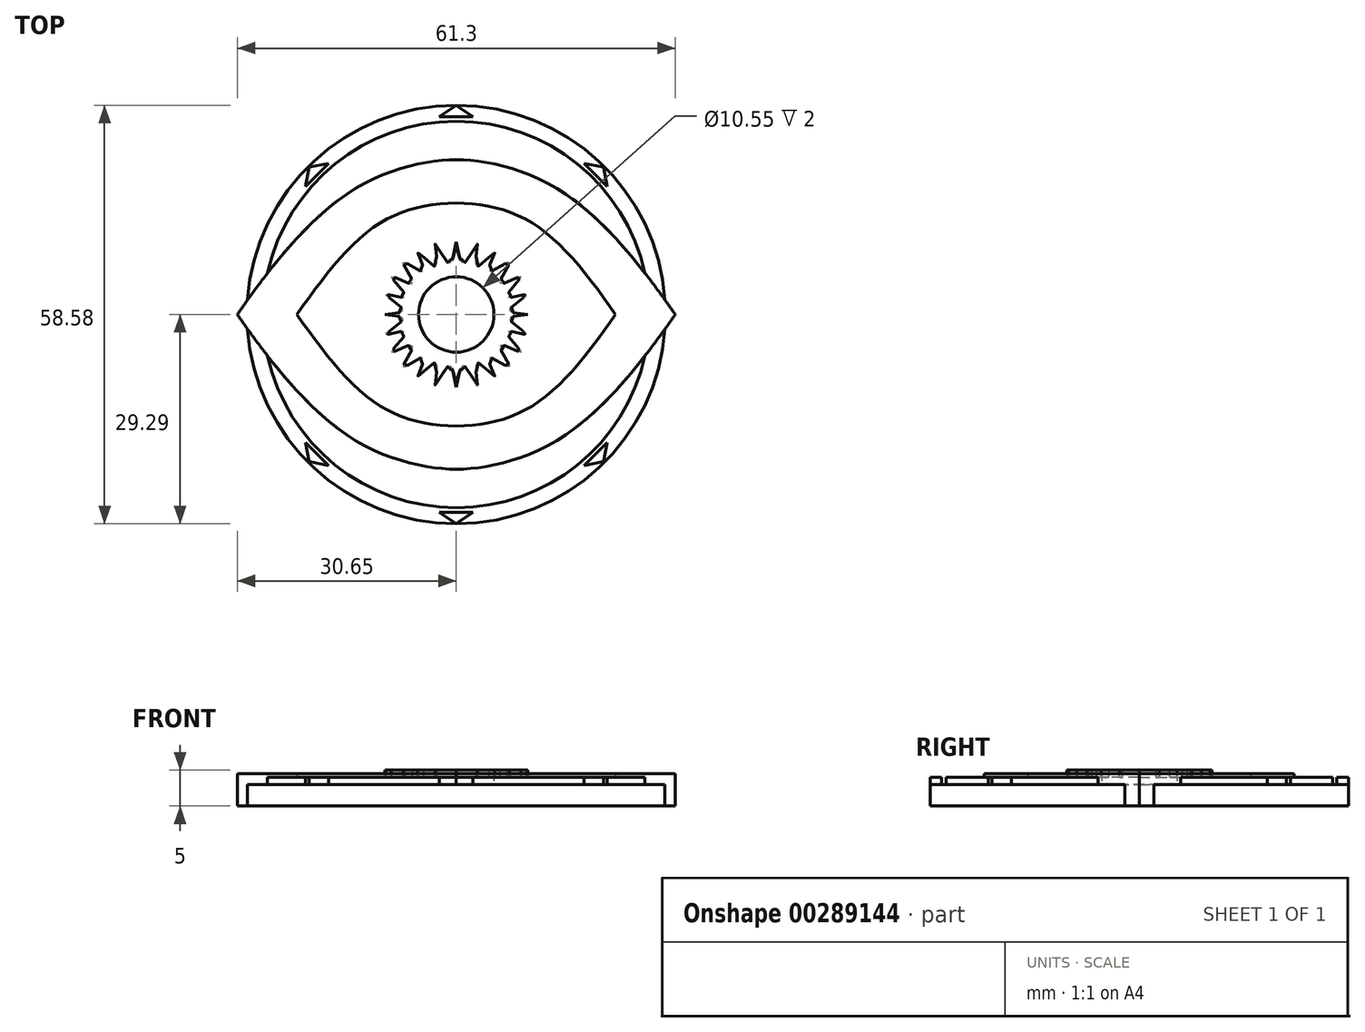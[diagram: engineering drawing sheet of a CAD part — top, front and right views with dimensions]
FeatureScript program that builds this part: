
annotation { "Feature Type Name" : "Feature", "Feature Type Description" : "" }
export const myFeature = defineFeature(function(context is Context, id is Id, definition is map)
    precondition{}
    {
        {
            var Q0;
            Q0=qCreatedBy(makeId("Top.planeOp"),FACE);
            var sketch = newSketch(context, id + "F0", { "sketchPlane" : qUnion([Q0])});
            skArc(sketch, "E0", {"start": v(0, 5.28) * mm, "mid": v(-3.73, 3.73) * mm, "end": v(-5.28, 0) * mm});
            skFitSpline(sketch, "E1", {"points": [v(-10, 0) * mm, v(-7.54, 0.76) * mm, v(-9.83, 2.78) * mm, v(-7.12, 2.5) * mm, v(-9.06, 5.28) * mm, v(-6.15, 4.35) * mm, v(-7.43, 7.33) * mm, v(-4.62, 6.08) * mm, v(-5.38, 8.72) * mm, v(-2.93, 6.76) * mm, v(-2.95, 9.9) * mm, v(-1.17, 7.25) * mm, v(0, 10.15) * mm], "startDerivative": vector(52.2, 3.3) * mm, "endDerivative": vector(8.65, 55.16) * mm});
            skFitSpline(sketch, "E2", {"points": [v(-22.28, 0) * mm, v(-11.02, 12.56) * mm, v(0, 15.6) * mm], "startDerivative": vector(19.04, 27.4) * mm, "endDerivative": vector(26.42, 0.51) * mm});
            skFitSpline(sketch, "E3", {"points": [v(-30.65, 0) * mm, v(-15.05, 17.04) * mm, v(0, 21.68) * mm], "startDerivative": vector(19.04, 27.4) * mm, "endDerivative": vector(26.42, 0.51) * mm});
            skArc(sketch, "E4", {"start": v(0, 27.04) * mm, "mid": v(-19.12, 19.12) * mm, "end": v(-27.04, 0) * mm});
            skArc(sketch, "E5", {"start": v(0, 29.29) * mm, "mid": v(-20.7, 20.7) * mm, "end": v(-29.29, 0) * mm});
            skLineSegment(sketch, "E6", {"start": v(-20.6, 20.6) * mm, "end": v(-21.1, 17.91) * mm});
            skLineSegment(sketch, "E7", {"start": v(-21.1, 17.91) * mm, "end": v(-17.87, 21.15) * mm});
            skLineSegment(sketch, "E8", {"start": v(-17.87, 21.15) * mm, "end": v(-20.6, 20.6) * mm});
            skLineSegment(sketch, "E9", {"start": v(0, 29.29) * mm, "end": v(-2.36, 27.66) * mm});
            skLineSegment(sketch, "E10", {"start": v(-2.36, 27.66) * mm, "end": v(0, 27.66) * mm});
            skLineSegment(sketch, "E11", {"start": v(0, 29.29) * mm, "end": v(0, 0) * mm});
            skLineSegment(sketch, "E12", {"start": v(-30.65, 0) * mm, "end": v(0, 0) * mm});
            skSolve(sketch);
        }
        {
            var Q0;
            {var subQ0=sQuery(id+"F0.wireOp",EDGE,"E0");Q0=makeQuery(id+"F0.imprint","IMPRINT",FACE,{"disambiguationData":[TD([[makeQuery(id+"F0.imprint","IMPRINT",EDGE,{"derivedFrom":subQ0}),1.0]])]});}
            extrude(context, id + "F1", {"entities" : qUnion([Q0]), "depth" : 1 * mm});
        }
        {
            var Q0;
            {var subQ0=sQuery(id+"F0.wireOp",EDGE,"E0");Q0=makeQuery(id+"F0.imprint","IMPRINT",FACE,{"disambiguationData":[TD([[makeQuery(id+"F0.imprint","IMPRINT",EDGE,{"derivedFrom":subQ0}),-1.0]])]});}
            extrude(context, id + "F2", {"entities" : qUnion([Q0]), "operationType" : NewBodyOperationType.ADD, "depth" : 3 * mm});
        }
        {
            var Q0;
            {var subQ0=sQuery(id+"F0.wireOp",EDGE,"E1");Q0=makeQuery(id+"F0.imprint","IMPRINT",FACE,{"disambiguationData":[TD([[makeQuery(id+"F0.imprint","IMPRINT",EDGE,{"derivedFrom":subQ0}),1.0]])]});}
            extrude(context, id + "F3", {"entities" : qUnion([Q0]), "operationType" : NewBodyOperationType.ADD, "depth" : 2 * mm});
        }
        {
            var Q0;
            {var subQ1=sQuery(id+"F0.wireOp",EDGE,"E2");Q0=makeQuery(id+"F0.imprint","IMPRINT",FACE,{"disambiguationData":[TD([[makeQuery(id+"F0.imprint","IMPRINT",EDGE,{"derivedFrom":subQ1}),1.0]])]});}
            var Q1;
            {var subQ0=sQuery(id+"F0.wireOp",EDGE,"E5");var subQ1=sQuery(id+"F0.wireOp",EDGE,"E3");var subQ2=makeQuery(id+"F0.imprint","INTERSECT",VERTEX,{"derivedFrom":[subQ1,subQ0]});Q1=makeQuery(id+"F0.imprint","IMPRINT",FACE,{"disambiguationData":[TD([[makeQuery(id+"F0.imprint","IMPRINT",EDGE,{"disambiguationData":[TD([[subQ2,-1.0]])],"derivedFrom":subQ1}),-1.0]])]});}
            var Q2;
            {var subQ0=sQuery(id+"F0.wireOp",EDGE,"E12");var subQ1=sQuery(id+"F0.wireOp",EDGE,"E3");var subQ2=makeQuery(id+"F0.imprint","INTERSECT",VERTEX,{"derivedFrom":[subQ1,subQ0]});Q2=makeQuery(id+"F0.imprint","IMPRINT",FACE,{"disambiguationData":[TD([[makeQuery(id+"F0.imprint","IMPRINT",EDGE,{"disambiguationData":[TD([[subQ2,-1.0]])],"derivedFrom":subQ1}),-1.0]])]});}
            extrude(context, id + "F4", {"entities" : qUnion([Q0, Q1, Q2]), "operationType" : NewBodyOperationType.ADD, "depth" : 2.5 * mm});
        }
        {
            var Q0;
            {var subQ0=sQuery(id+"F0.wireOp",EDGE,"E11");var subQ1=sQuery(id+"F0.wireOp",EDGE,"E3");var subQ2=makeQuery(id+"F0.imprint","INTERSECT",VERTEX,{"derivedFrom":[subQ1,subQ0]});Q0=makeQuery(id+"F0.imprint","IMPRINT",FACE,{"disambiguationData":[TD([[makeQuery(id+"F0.imprint","IMPRINT",EDGE,{"disambiguationData":[TD([[subQ2,1.0]])],"derivedFrom":subQ1}),1.0]])]});}
            extrude(context, id + "F5", {"entities" : qUnion([Q0]), "operationType" : NewBodyOperationType.ADD, "depth" : 2 * mm});
        }
        {
            var Q0;
            Q0=makeQuery(id+"F0.imprint","IMPRINT",FACE,{"disambiguationData":[TD([[makeQuery(id+"F0.imprint","IMPRINT",EDGE,{"derivedFrom":sQuery(id+"F0.wireOp",EDGE,"E6")}),-1.0]])]});
            extrude(context, id + "F6", {"entities" : qUnion([Q0]), "operationType" : NewBodyOperationType.ADD, "depth" : 1 * mm});
        }
        {
            var Q0;
            Q0=makeQuery(id+"F0.imprint","IMPRINT",FACE,{"disambiguationData":[TD([[makeQuery(id+"F0.imprint","IMPRINT",EDGE,{"derivedFrom":sQuery(id+"F0.wireOp",EDGE,"E6")}),1.0]])]});
            var Q1;
            {var subQ0=sQuery(id+"F0.wireOp",EDGE,"E9");Q1=makeQuery(id+"F0.imprint","IMPRINT",FACE,{"disambiguationData":[TD([[makeQuery(id+"F0.imprint","IMPRINT",EDGE,{"derivedFrom":subQ0}),1.0]])]});}
            extrude(context, id + "F7", {"entities" : qUnion([Q0, Q1]), "operationType" : NewBodyOperationType.ADD, "depth" : 2 * mm});
        }
        {
            var Q0;
            Q0=makeQuery(id+"F1.opExtrude","SWEPT_BODY",BODY,{"disambiguationData":[OSD([sQuery(id+"F0.wireOp",EDGE,"E0"),sQuery(id+"F0.wireOp",EDGE,"E11"),sQuery(id+"F0.wireOp",EDGE,"E12")])]});
            var Q1;
            Q1=qCreatedBy(makeId("Right.planeOp"),FACE);
            mirror(context, id + "F8", {"operationType" : NewBodyOperationType.ADD, "entities" : qUnion([Q0]), "mirrorPlane" : qUnion([Q1])});
        }
        {
            var Q0;
            Q0=makeQuery(id+"F1.opExtrude","SWEPT_BODY",BODY,{"disambiguationData":[OSD([sQuery(id+"F0.wireOp",EDGE,"E0"),sQuery(id+"F0.wireOp",EDGE,"E11"),sQuery(id+"F0.wireOp",EDGE,"E12")])]});
            var Q1;
            Q1=qCreatedBy(makeId("Front.planeOp"),FACE);
            mirror(context, id + "F9", {"operationType" : NewBodyOperationType.ADD, "entities" : qUnion([Q0]), "mirrorPlane" : qUnion([Q1])});
        }
        {
            var Q0;
            {var subQ0=sQuery(id+"F0.wireOp",EDGE,"E11");var subQ1=sQuery(id+"F0.wireOp",EDGE,"E10");var subQ2=sQuery(id+"F0.wireOp",EDGE,"E9");var subQ3=sQuery(id+"F0.wireOp",EDGE,"E8");var subQ4=sQuery(id+"F0.wireOp",EDGE,"E7");var subQ5=sQuery(id+"F0.wireOp",EDGE,"E6");var subQ6=sQuery(id+"F0.wireOp",EDGE,"E4");var subQ7=sQuery(id+"F0.wireOp",EDGE,"E3");var subQ8=sQuery(id+"F0.wireOp",EDGE,"E12");var subQ9=sQuery(id+"F0.wireOp",EDGE,"E2");var subQ10=sQuery(id+"F0.wireOp",EDGE,"E1");var subQ11=sQuery(id+"F0.wireOp",EDGE,"E0");var subQ12=makeQuery(id+"F7.boolean.opBoolean","MERGE",FACE,{"derivedFrom":[makeQuery(id+"F6.boolean.opBoolean","MERGE",FACE,{"derivedFrom":[makeQuery(id+"F5.boolean.opBoolean","MERGE",FACE,{"derivedFrom":[makeQuery(id+"F4.boolean.opBoolean","MERGE",FACE,{"derivedFrom":[makeQuery(id+"F3.boolean.opBoolean","MERGE",FACE,{"derivedFrom":[makeQuery(id+"F2.boolean.opBoolean","MERGE",FACE,{"derivedFrom":[makeQuery(id+"F1.opExtrude","CAP_FACE",FACE,{"disambiguationData":[OSD([subQ11,subQ0,subQ8])],"isStart":true}),makeQuery(id+"F2.opExtrude","CAP_FACE",FACE,{"disambiguationData":[OSD([subQ11,subQ10,subQ0,subQ8])],"isStart":true})]}),makeQuery(id+"F3.opExtrude","CAP_FACE",FACE,{"disambiguationData":[OSD([subQ10,subQ9,subQ0,subQ8])],"isStart":true})]}),makeQuery(id+"F4.opExtrude","CAP_FACE",FACE,{"disambiguationData":[OSD([subQ9,subQ7,subQ0,subQ8])],"isStart":true})]}),makeQuery(id+"F5.opExtrude","CAP_FACE",FACE,{"disambiguationData":[OSD([subQ7,subQ6,subQ0])],"isStart":true})]}),makeQuery(id+"F6.opExtrude","CAP_FACE",FACE,{"disambiguationData":[OSD([subQ7,subQ6,sQuery(id+"F0.wireOp",EDGE,"E5"),subQ5,subQ4,subQ3,subQ2,subQ1,subQ0])],"isStart":true})]}),makeQuery(id+"F7.opExtrude","CAP_FACE",FACE,{"disambiguationData":[OSD([subQ5,subQ4,subQ3])],"isStart":true}),makeQuery(id+"F7.opExtrude","CAP_FACE",FACE,{"disambiguationData":[OSD([subQ2,subQ1,subQ0])],"isStart":true})]});var subQ13=makeQuery(id+"F8.boolean.opBoolean","MERGE",FACE,{"derivedFrom":[subQ12,makeQuery(id+"F8.opPattern","COPY",FACE,{"derivedFrom":subQ12,"instanceName":"1"})]});Q0=makeQuery(id+"F9.boolean.opBoolean","MERGE",FACE,{"derivedFrom":[subQ13,makeQuery(id+"F9.opPattern","COPY",FACE,{"derivedFrom":subQ13,"instanceName":"1"})]});}
            extrude(context, id + "F10", {"entities" : qUnion([Q0]), "operationType" : NewBodyOperationType.ADD, "depth" : 2 * mm});
        }
    });
